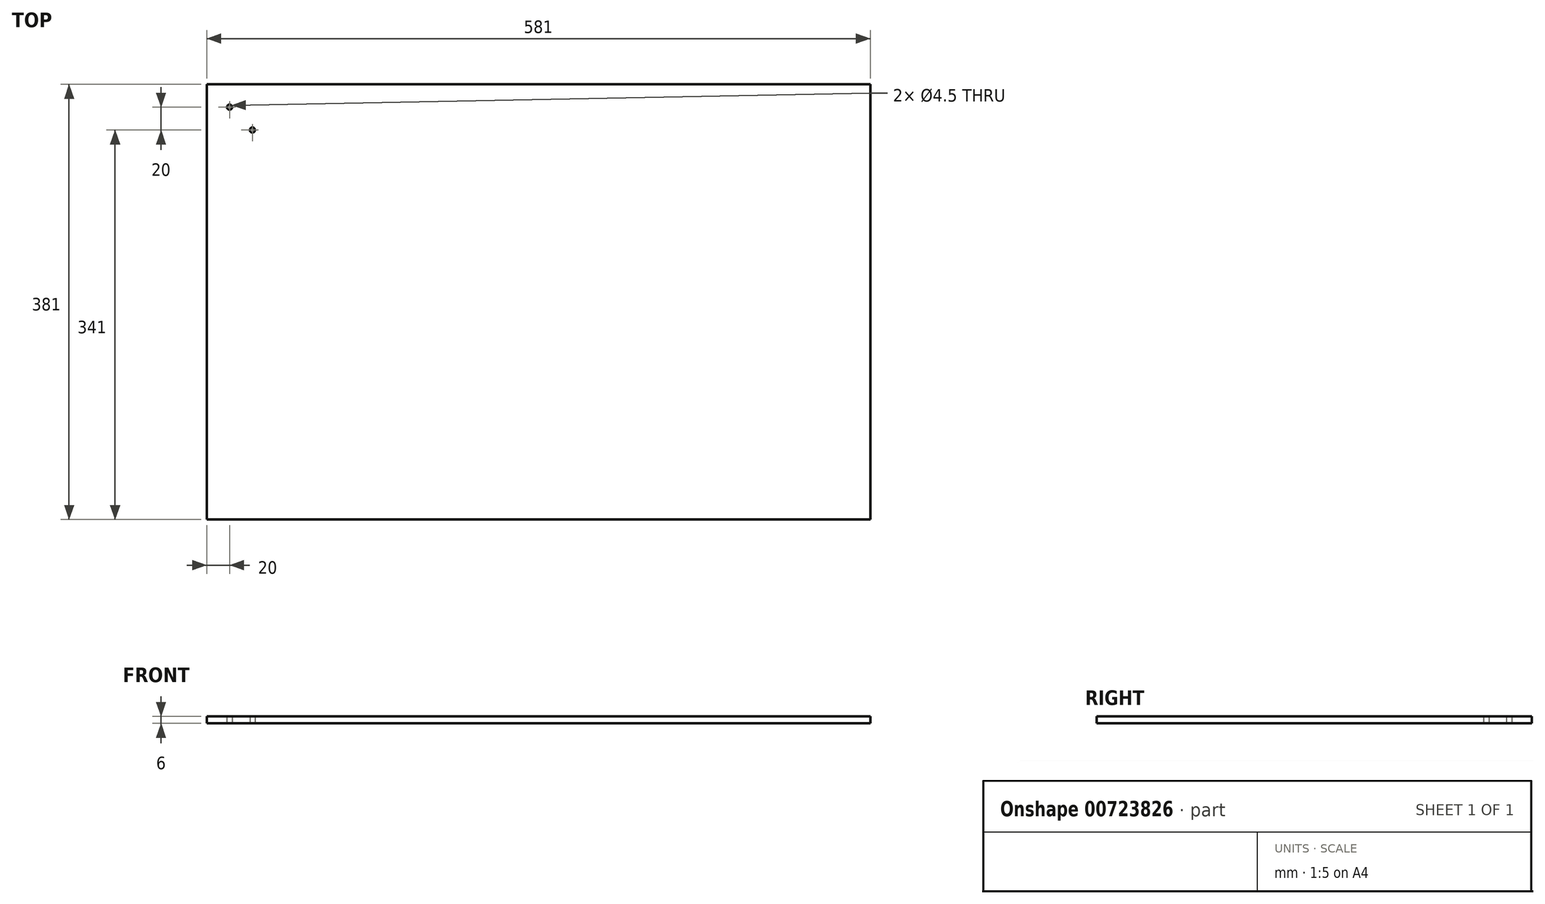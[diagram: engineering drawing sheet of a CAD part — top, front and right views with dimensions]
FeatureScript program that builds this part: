
annotation { "Feature Type Name" : "Feature", "Feature Type Description" : "" }
export const myFeature = defineFeature(function(context is Context, id is Id, definition is map)
    precondition{}
    {
        {
            var Q0;
            Q0=qCreatedBy(makeId("Top.planeOp"),FACE);
            var sketch = newSketch(context, id + "F0", { "sketchPlane" : qUnion([Q0])});
            skLineSegment(sketch, "E0.bottom", {"start": v(290.5, 190.5) * mm, "end": v(-290.5, 190.5) * mm});
            skLineSegment(sketch, "E0.top", {"start": v(290.5, -190.5) * mm, "end": v(-290.5, -190.5) * mm});
            skLineSegment(sketch, "E0.left", {"start": v(290.5, 190.5) * mm, "end": v(290.5, -190.5) * mm});
            skLineSegment(sketch, "E0.right", {"start": v(-290.5, 190.5) * mm, "end": v(-290.5, -190.5) * mm});
            skPoint(sketch, "E0.middle", {"position": v(0, 0) * mm});
            skPoint(sketch, "E1", {"position": v(-270.5, 170.5) * mm});
            skPoint(sketch, "E2", {"position": v(-250.5, 150.5) * mm});
            skSolve(sketch);
        }
        {
            var Q0;
            Q0 = qSketchRegion(id + "F0", true);
            extrude(context, id + "F1", {"entities" : qUnion([Q0]), "depth" : 6 * mm, "offsetDistance" : 25 * mm});
        }
        {
            var Q0;
            Q0=sQuery(id+"F0.wireOp",VERTEX,"E2");
            var Q1;
            Q1=sQuery(id+"F0.wireOp",VERTEX,"E1");
            var Q2;
            Q2=makeQuery(id+"F1.opExtrude","SWEPT_BODY",BODY,{"disambiguationData":[OSD([sQuery(id+"F0.wireOp",EDGE,"E0.bottom"),sQuery(id+"F0.wireOp",EDGE,"E0.top"),sQuery(id+"F0.wireOp",EDGE,"E0.left"),sQuery(id+"F0.wireOp",EDGE,"E0.right")])]});
            hole(context, id + "F2", {"style" : HoleStyle.SIMPLE, "endStyle" : HoleEndStyle.THROUGH, "oppositeDirection" : true, "holeDiameter" : 4.5 * mm, "majorDiameter" : 5 * mm, "isTappedThrough" : true, "tappedDepth" : 12 * mm, "tapClearance" : 3, "locations" : qUnion([Q0, Q1]), "scope" : qUnion([Q2])});
        }
    });
